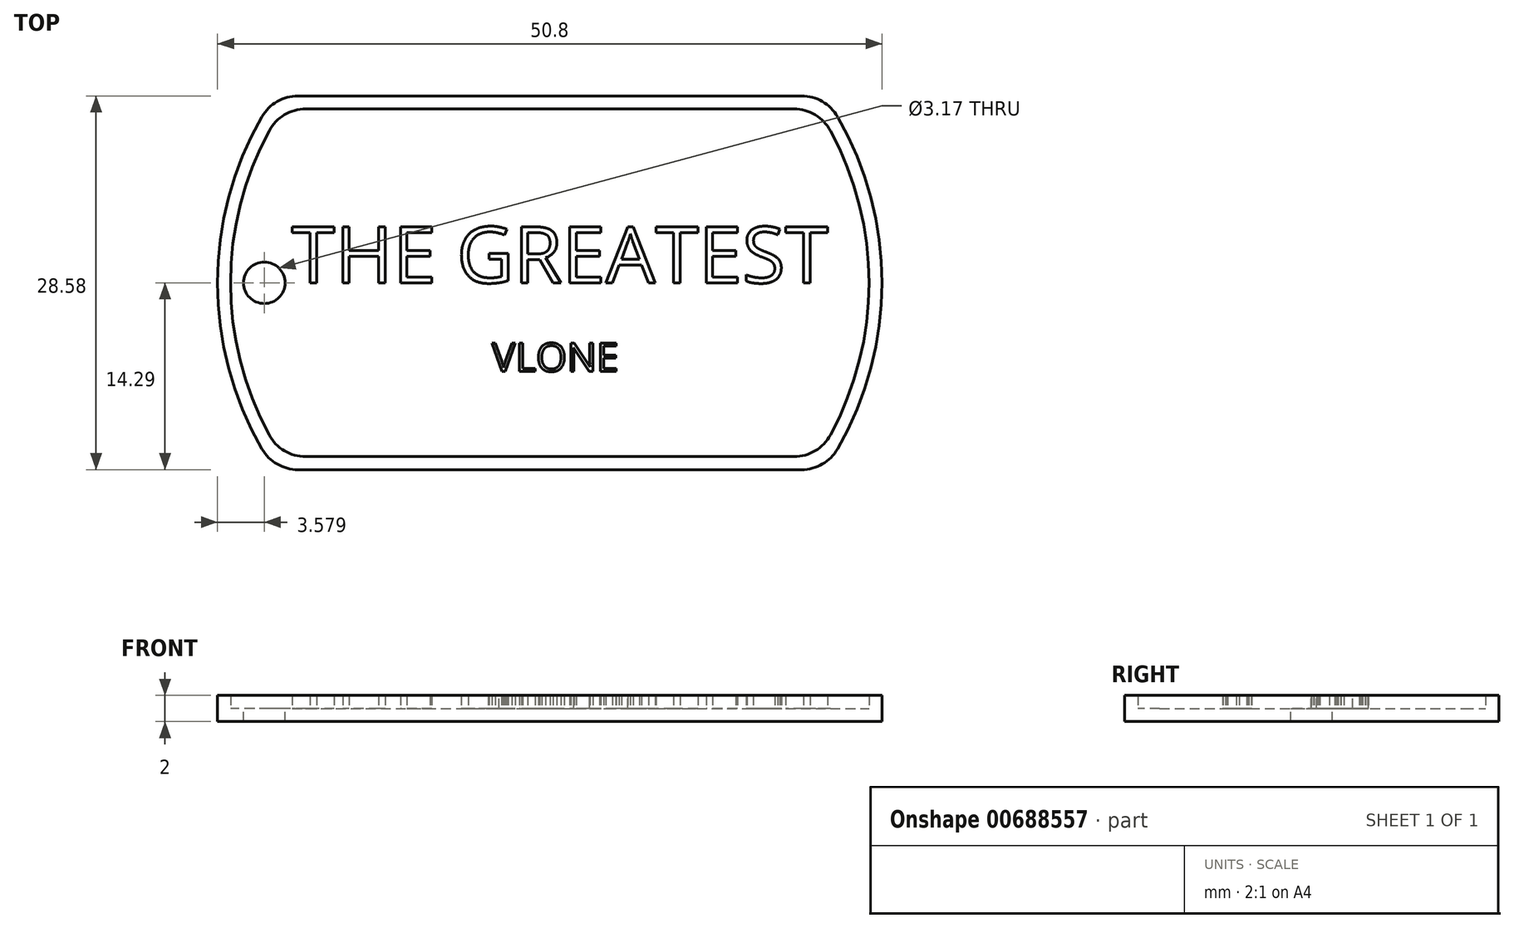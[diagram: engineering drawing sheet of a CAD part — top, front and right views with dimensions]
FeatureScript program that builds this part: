
annotation { "Feature Type Name" : "Feature", "Feature Type Description" : "" }
export const myFeature = defineFeature(function(context is Context, id is Id, definition is map)
    precondition{}
    {
        {
            var Q0;
            Q0=qCreatedBy(makeId("Top.planeOp"),FACE);
            var sketch = newSketch(context, id + "F0", { "sketchPlane" : qUnion([Q0])});
            skArc(sketch, "E0", {"start": v(-22, 12.7) * mm, "mid": v(-25.4, 0) * mm, "end": v(-22, -12.7) * mm});
            skLineSegment(sketch, "E1.top", {"start": v(-19.25, -14.29) * mm, "end": v(19.25, -14.29) * mm});
            skArc(sketch, "E2.trimOffspring", {"start": v(22, -12.7) * mm, "mid": v(25.4, 0) * mm, "end": v(22, 12.7) * mm});
            skLineSegment(sketch, "E3", {"start": v(-19.25, 14.29) * mm, "end": v(19.25, 14.29) * mm});
            skPoint(sketch, "E4.visualSharp", {"position": v(-21, 14.29) * mm});
            skArc(sketch, "E4.filletArc", {"start": v(-19.25, 14.29) * mm, "mid": v(-20.83, 13.86) * mm, "end": v(-22, 12.7) * mm});
            skPoint(sketch, "E5.visualSharp", {"position": v(21, 14.29) * mm});
            skArc(sketch, "E5.filletArc", {"start": v(22, 12.7) * mm, "mid": v(20.83, 13.86) * mm, "end": v(19.25, 14.29) * mm});
            skPoint(sketch, "E6.visualSharp", {"position": v(21, -14.29) * mm});
            skArc(sketch, "E6.filletArc", {"start": v(19.25, -14.29) * mm, "mid": v(20.83, -13.86) * mm, "end": v(22, -12.7) * mm});
            skPoint(sketch, "E7.visualSharp", {"position": v(-21, -14.29) * mm});
            skArc(sketch, "E7.filletArc", {"start": v(-22, -12.7) * mm, "mid": v(-20.83, -13.86) * mm, "end": v(-19.25, -14.29) * mm});
            skSolve(sketch);
        }
        {
            var Q0;
            Q0=makeQuery(id+"F0.imprint","IMPRINT",FACE,{"disambiguationData":[TD([[makeQuery(id+"F0.imprint","IMPRINT",EDGE,{"derivedFrom":sQuery(id+"F0.wireOp",EDGE,"E0")}),1.0]])]});
            extrude(context, id + "F1", {"entities" : qUnion([Q0]), "depth" : 1 * mm, "offsetDistance" : 25.4 * mm});
        }
        {
            var Q0;
            Q0=makeQuery(id+"F1.opExtrude","CAP_FACE",FACE,{"disambiguationData":[OSD([sQuery(id+"F0.wireOp",EDGE,"E0"),sQuery(id+"F0.wireOp",EDGE,"E1.top"),sQuery(id+"F0.wireOp",EDGE,"E2.trimOffspring"),sQuery(id+"F0.wireOp",EDGE,"E3"),sQuery(id+"F0.wireOp",EDGE,"E4.filletArc"),sQuery(id+"F0.wireOp",EDGE,"E5.filletArc"),sQuery(id+"F0.wireOp",EDGE,"E6.filletArc"),sQuery(id+"F0.wireOp",EDGE,"E7.filletArc")])],"isStart":false});
            var sketch = newSketch(context, id + "F2", { "sketchPlane" : qUnion([Q0])});
            skLineSegment(sketch, "E8.0", {"start": v(-18.66, 13.29) * mm, "end": v(18.66, 13.29) * mm});
            skArc(sketch, "E8.1", {"start": v(-21.45, 11.63) * mm, "mid": v(-24.4, 0) * mm, "end": v(-21.45, -11.63) * mm});
            skLineSegment(sketch, "E8.2", {"start": v(-18.66, -13.29) * mm, "end": v(18.66, -13.29) * mm});
            skArc(sketch, "E8.3", {"start": v(21.45, -11.63) * mm, "mid": v(24.4, 0) * mm, "end": v(21.45, 11.63) * mm});
            skPoint(sketch, "E9.visualSharp", {"position": v(-20.46, 13.29) * mm});
            skArc(sketch, "E9.filletArc", {"start": v(-18.66, 13.29) * mm, "mid": v(-20.29, 12.84) * mm, "end": v(-21.45, 11.63) * mm});
            skPoint(sketch, "E10.visualSharp", {"position": v(20.46, 13.29) * mm});
            skArc(sketch, "E10.filletArc", {"start": v(21.45, 11.63) * mm, "mid": v(20.29, 12.84) * mm, "end": v(18.66, 13.29) * mm});
            skPoint(sketch, "E11.visualSharp", {"position": v(20.46, -13.29) * mm});
            skArc(sketch, "E11.filletArc", {"start": v(18.66, -13.29) * mm, "mid": v(20.29, -12.84) * mm, "end": v(21.45, -11.63) * mm});
            skPoint(sketch, "E12.visualSharp", {"position": v(-20.46, -13.29) * mm});
            skArc(sketch, "E12.filletArc", {"start": v(-21.45, -11.63) * mm, "mid": v(-20.29, -12.84) * mm, "end": v(-18.66, -13.29) * mm});
            skLineSegment(sketch, "E13.0", {"start": v(-19.25, 14.29) * mm, "end": v(19.25, 14.29) * mm});
            skArc(sketch, "E13.1", {"start": v(-22, 12.7) * mm, "mid": v(-25.4, 0) * mm, "end": v(-22, -12.7) * mm});
            skLineSegment(sketch, "E13.2", {"start": v(-19.25, -14.29) * mm, "end": v(19.25, -14.29) * mm});
            skArc(sketch, "E13.3", {"start": v(22, -12.7) * mm, "mid": v(25.4, 0) * mm, "end": v(22, 12.7) * mm});
            skPoint(sketch, "E14.visualSharp", {"position": v(-21, -14.29) * mm});
            skArc(sketch, "E14.filletArc", {"start": v(-22, -12.7) * mm, "mid": v(-20.83, -13.86) * mm, "end": v(-19.25, -14.29) * mm});
            skPoint(sketch, "E15.visualSharp", {"position": v(21, -14.29) * mm});
            skArc(sketch, "E15.filletArc", {"start": v(19.25, -14.29) * mm, "mid": v(20.83, -13.86) * mm, "end": v(22, -12.7) * mm});
            skPoint(sketch, "E16.visualSharp", {"position": v(21, 14.29) * mm});
            skArc(sketch, "E16.filletArc", {"start": v(22, 12.7) * mm, "mid": v(20.83, 13.86) * mm, "end": v(19.25, 14.29) * mm});
            skPoint(sketch, "E17.visualSharp", {"position": v(-21, 14.29) * mm});
            skArc(sketch, "E17.filletArc", {"start": v(-19.25, 14.29) * mm, "mid": v(-20.83, 13.86) * mm, "end": v(-22, 12.7) * mm});
            skSolve(sketch);
        }
        {
            var Q0;
            Q0=makeQuery(id+"F2.imprint","IMPRINT",FACE,{"disambiguationData":[TD([[makeQuery(id+"F2.imprint","IMPRINT",EDGE,{"derivedFrom":sQuery(id+"F2.wireOp",EDGE,"E8.0")}),1.0]])]});
            extrude(context, id + "F3", {"entities" : qUnion([Q0]), "operationType" : NewBodyOperationType.ADD, "depth" : 1 * mm, "offsetDistance" : 25.4 * mm});
        }
        {
            var Q0;
            Q0=makeQuery(id+"F1.opExtrude","CAP_FACE",FACE,{"disambiguationData":[OSD([sQuery(id+"F0.wireOp",EDGE,"E0"),sQuery(id+"F0.wireOp",EDGE,"E1.top"),sQuery(id+"F0.wireOp",EDGE,"E2.trimOffspring"),sQuery(id+"F0.wireOp",EDGE,"E3"),sQuery(id+"F0.wireOp",EDGE,"E4.filletArc"),sQuery(id+"F0.wireOp",EDGE,"E5.filletArc"),sQuery(id+"F0.wireOp",EDGE,"E6.filletArc"),sQuery(id+"F0.wireOp",EDGE,"E7.filletArc")])],"isStart":false});
            var sketch = newSketch(context, id + "F4", { "sketchPlane" : qUnion([Q0])});
            skCircle(sketch, "E18", {"center": v(-21.82, 0) * mm, "radius": 1.59 * mm});
            skSolve(sketch);
        }
        {
            var Q0;
            Q0=makeQuery(id+"F4.imprint","IMPRINT",FACE,{"disambiguationData":[TD([[makeQuery(id+"F4.imprint","IMPRINT",EDGE,{"derivedFrom":sQuery(id+"F4.wireOp",EDGE,"E18")}),1.0]])]});
            extrude(context, id + "F5", {"entities" : qUnion([Q0]), "operationType" : NewBodyOperationType.REMOVE, "oppositeDirection" : true, "depth" : 1 * mm, "offsetDistance" : 25.4 * mm});
        }
        {
            var Q0;
            Q0=makeQuery(id+"F4.imprint","IMPRINT",FACE,{"disambiguationData":[TD([[makeQuery(id+"F4.imprint","IMPRINT",EDGE,{"derivedFrom":sQuery(id+"F4.wireOp",EDGE,"E18")}),-1.0]])]});
            var sketch = newSketch(context, id + "F6", { "sketchPlane" : qUnion([Q0])});
            skText(sketch, "E19", { "text": "THE GREATEST", "fontName": "OpenSans-Regular.ttf"});
            skText(sketch, "E20", { "text": "VLONE", "fontName": "OpenSans-Regular.ttf"});
            const initialGuessF6  = {"E19": [-0.01973, 0, 1, 0, 0.00431], "E20": [-0.00443, -0.00678, 1, 0, 0.00218]};
            skSetInitialGuess(sketch, initialGuessF6);
            skSolve(sketch);
        }
        {
            var Q0;
            Q0 = qSketchRegion(id + "F6", true);
            extrude(context, id + "F7", {"entities" : qUnion([Q0]), "operationType" : NewBodyOperationType.ADD, "depth" : 1 * mm, "offsetDistance" : 25.4 * mm});
        }
    });
